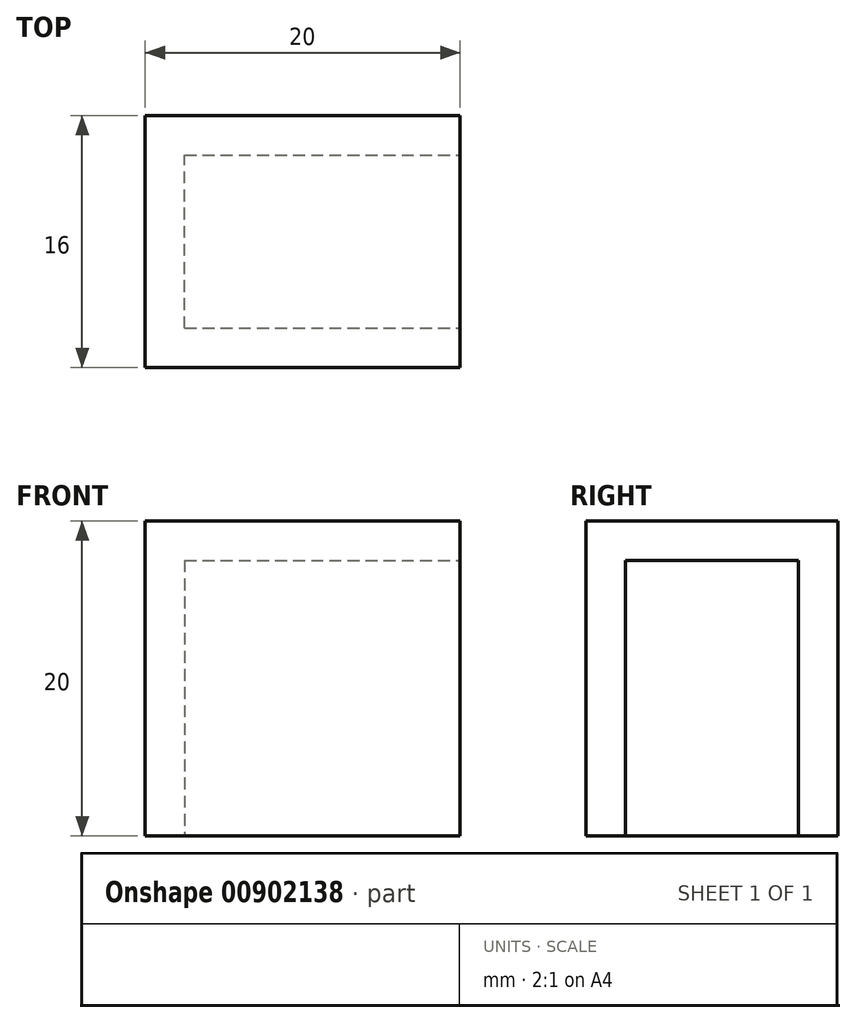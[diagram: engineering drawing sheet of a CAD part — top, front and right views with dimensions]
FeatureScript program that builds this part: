
annotation { "Feature Type Name" : "Feature", "Feature Type Description" : "" }
export const myFeature = defineFeature(function(context is Context, id is Id, definition is map)
    precondition{}
    {
        {
            var Q0;
            Q0=qCreatedBy(makeId("Front.planeOp"),FACE);
            var sketch = newSketch(context, id + "F0", { "sketchPlane" : qUnion([Q0])});
            skLineSegment(sketch, "E0.bottom", {"start": v(-10, 10) * mm, "end": v(10, 10) * mm});
            skLineSegment(sketch, "E0.top", {"start": v(-10, -10) * mm, "end": v(10, -10) * mm});
            skLineSegment(sketch, "E0.left", {"start": v(-10, 10) * mm, "end": v(-10, -10) * mm});
            skLineSegment(sketch, "E0.right", {"start": v(10, 10) * mm, "end": v(10, -10) * mm});
            skPoint(sketch, "E0.middle", {"position": v(0, 0) * mm});
            skSolve(sketch);
        }
        {
            var Q0;
            Q0=makeQuery(id+"F0.imprint","IMPRINT",FACE,{"disambiguationData":[TD([[makeQuery(id+"F0.imprint","IMPRINT",EDGE,{"derivedFrom":sQuery(id+"F0.wireOp",EDGE,"E0.bottom")}),-1.0]])]});
            extrude(context, id + "F1", {"entities" : qUnion([Q0]), "depth" : 16 * mm, "offsetDistance" : 25 * mm});
        }
        {
            var Q0;
            Q0=makeQuery(id+"F1.opExtrude","SWEPT_FACE",FACE,{"disambiguationData":[OSD([sQuery(id+"F0.wireOp",EDGE,"E0.top")])]});
            var Q1;
            Q1=makeQuery(id+"F1.opExtrude","SWEPT_FACE",FACE,{"disambiguationData":[OSD([sQuery(id+"F0.wireOp",EDGE,"E0.right")])]});
            shell(context, id + "F2", {"entities" : qUnion([Q0, Q1]), "thickness" : 2.5 * mm});
        }
    });
